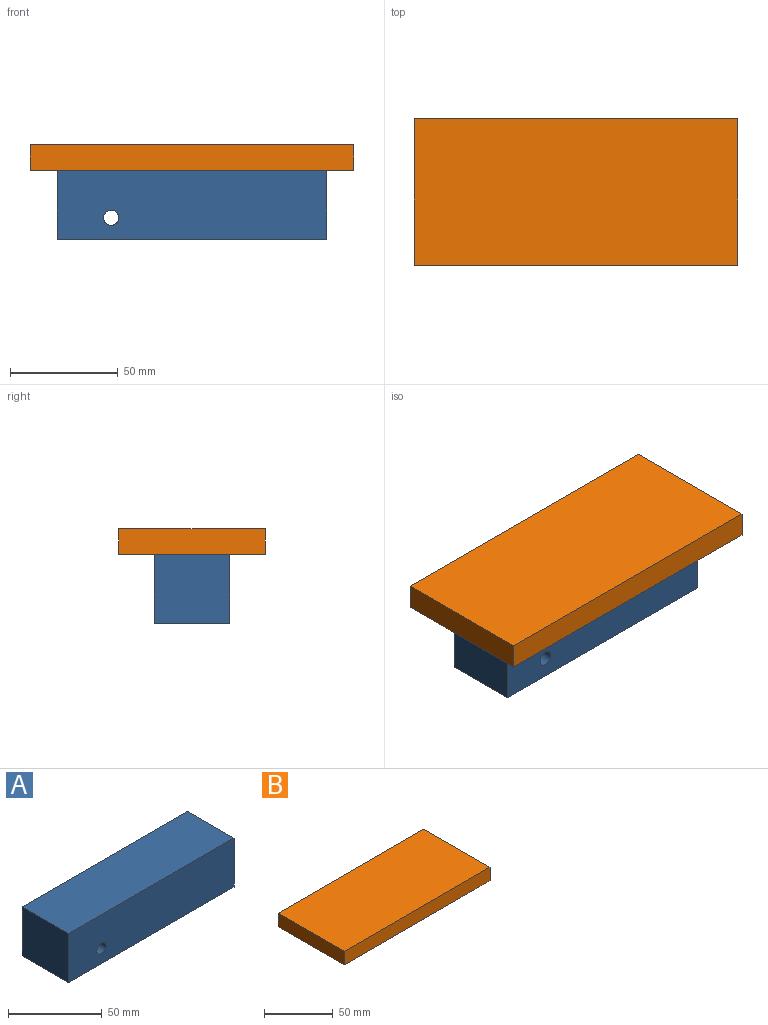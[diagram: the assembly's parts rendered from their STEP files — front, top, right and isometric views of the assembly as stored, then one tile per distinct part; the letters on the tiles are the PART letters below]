
ASSEMBLY  parts=2 mates=2
PART A: 7 faces, bbox 125x35x32 mm
  f0: plane 125x35mm, normal (0,0,-1), area 4375mm2, adj f1,f4,f5,f6
  f1: plane 35x32mm, normal (1,0,0), area 1120mm2, adj f0,f2,f5,f6
  f2: plane 125x35mm, normal (0,0,1), area 4375mm2, adj f1,f4,f5,f6
  f3: cylinder r=3.5mm len=35mm, axis (0,1,0), area 769.7mm2, adj f5,f6
  f4: plane 35x32mm, normal (-1,0,0), area 1120mm2, adj f0,f2,f5,f6
  f5: plane 125x32mm, normal (0,-1,0), area 3961.5mm2, adj f0,f1,f2,f3,f4
  f6: plane 125x32mm, normal (0,1,0), area 3961.5mm2, adj f0,f1,f2,f3,f4
PART B: 6 faces, bbox 150x68x12 mm
  f0: plane 150x12mm, normal (0,-1,0), area 1800mm2, adj f1,f3,f4,f5
  f1: plane 68x12mm, normal (-1,0,0), area 816mm2, adj f0,f2,f4,f5
  f2: plane 150x12mm, normal (0,1,0), area 1800mm2, adj f1,f3,f4,f5
  f3: plane 68x12mm, normal (1,0,0), area 816mm2, adj f0,f2,f4,f5
  f4: plane 150x68mm, normal (0,0,-1), area 10200mm2, adj f0,f1,f2,f3
  f5: plane 150x68mm, normal (0,0,1), area 10200mm2, adj f0,f1,f2,f3
PLACE A t=(14.43,5.9,8.23)mm fixed
PLACE B t=(-130.63,-10.6,52.23)mm
MATE fastened A.f2 <-> B.f4  axis (0,0,1) through (-48.07,-11.6,40.23)mm
MATE fastened A.f2 <-> A.f2  axis (0,0,1) through (-48.07,5.9,40.23)mm
